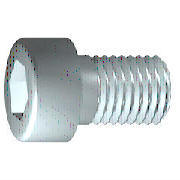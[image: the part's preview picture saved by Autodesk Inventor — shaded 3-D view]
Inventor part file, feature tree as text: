
AUTODESK INVENTOR PART (.ipt)
format: ipt  version: 2020 (Build 240168000, 168)  size: 193,024 bytes
history: native  units: mm (DEFAULTED — no unit token found)
features: sketch x2, extrude x1, plane x1, fillet x1
ambient origin geometry x7: Origin, YZ Plane, XY Plane, X Axis, Y Axis, Z Axis, Center Point
bodies: Solid1 (feature_tree), Body (feature_tree)
feature tree (5):
  extrude  "Slot"  Depth=2.0mm
  plane  "Work Plane1"
  fillet  "Fillet2"  Radius=2.0mm
  sketch  "Sketch1"  dims[d1=14.5mm d2=0.306825mm d3=2.0mm]
  sketch  "Sketch2"  dims[d4=1.5mm d5=60.0deg d6=3.0mm d7=3.0mm d8=2.309401mm d9=5.5mm d10=90.0deg d11=10.0mm d12=0.0mm d13=14.5mm d14=0.0mm d15=0.306725mm d16=0.306725mm d17=0.3mm d19=0.0mm d26=16.0mm d27=45.0deg d28=0.0mm d29=0.0mm d30=0.1mm]
